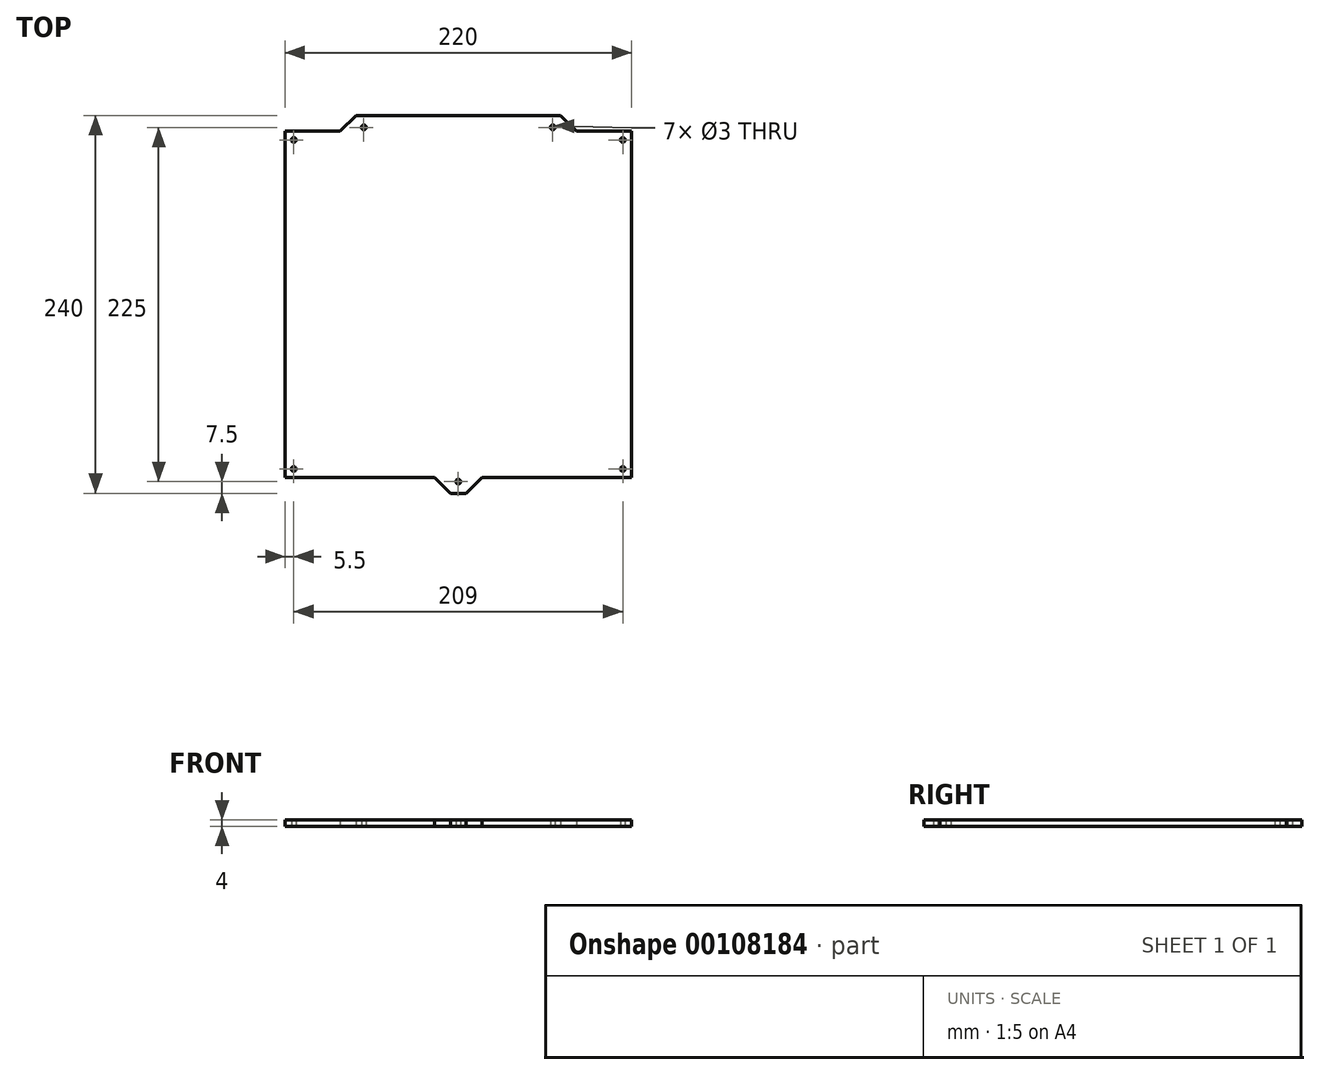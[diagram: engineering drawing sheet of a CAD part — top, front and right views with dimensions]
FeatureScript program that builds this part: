
annotation { "Feature Type Name" : "Feature", "Feature Type Description" : "" }
export const myFeature = defineFeature(function(context is Context, id is Id, definition is map)
    precondition{}
    {
        {
            var Q0;
            Q0=qCreatedBy(makeId("Top.planeOp"),FACE);
            var sketch = newSketch(context, id + "F0", { "sketchPlane" : qUnion([Q0])});
            skLineSegment(sketch, "E0.bottom", {"start": v(-110, 110) * mm, "end": v(-75, 110) * mm});
            skLineSegment(sketch, "E0.top", {"start": v(-110, -110) * mm, "end": v(-15, -110) * mm});
            skLineSegment(sketch, "E0.left", {"start": v(-110, 110) * mm, "end": v(-110, -110) * mm});
            skPoint(sketch, "E0.middle", {"position": v(0, 0) * mm});
            skLineSegment(sketch, "E1", {"start": v(0, 120) * mm, "end": v(-65, 120) * mm});
            skLineSegment(sketch, "E2", {"start": v(-65, 120) * mm, "end": v(-75, 110) * mm});
            skLineSegment(sketch, "E3", {"start": v(0, -120) * mm, "end": v(-5, -120) * mm});
            skLineSegment(sketch, "E4", {"start": v(-5, -120) * mm, "end": v(-15, -110) * mm});
            skCircle(sketch, "E5", {"center": v(0, -112.5) * mm, "radius": 1.5 * mm});
            skCircle(sketch, "E6", {"center": v(-60, 112.5) * mm, "radius": 1.5 * mm});
            skCircle(sketch, "E7.MirrorC", {"center": v(60, 112.5) * mm, "radius": 1.5 * mm});
            skLineSegment(sketch, "E8.MirrorCS", {"start": v(0, 120) * mm, "end": v(65, 120) * mm});
            skLineSegment(sketch, "E9.MirrorCS", {"start": v(65, 120) * mm, "end": v(75, 110) * mm});
            skLineSegment(sketch, "E10.MirrorCS", {"start": v(110, 110) * mm, "end": v(75, 110) * mm});
            skLineSegment(sketch, "E11.MirrorCS", {"start": v(110, 110) * mm, "end": v(110, -110) * mm});
            skLineSegment(sketch, "E12.MirrorCS", {"start": v(110, -110) * mm, "end": v(15, -110) * mm});
            skLineSegment(sketch, "E13.MirrorCS", {"start": v(0, -120) * mm, "end": v(5, -120) * mm});
            skLineSegment(sketch, "E14.MirrorCS", {"start": v(5, -120) * mm, "end": v(15, -110) * mm});
            skCircle(sketch, "E15", {"center": v(-104.5, 104.5) * mm, "radius": 1.5 * mm});
            skCircle(sketch, "E16.MirrorC", {"center": v(104.5, 104.5) * mm, "radius": 1.5 * mm});
            skCircle(sketch, "E17.MirrorC", {"center": v(-104.5, -104.5) * mm, "radius": 1.5 * mm});
            skCircle(sketch, "E18.MirrorC", {"center": v(104.5, -104.5) * mm, "radius": 1.5 * mm});
            skSolve(sketch);
        }
        {
            var Q0;
            {var subQ1=sQuery(id+"F0.wireOp",EDGE,"E0.left");Q0=makeQuery(id+"F0.imprint","IMPRINT",FACE,{"disambiguationData":[TD([[makeQuery(id+"F0.imprint","IMPRINT",EDGE,{"derivedFrom":subQ1}),1.0]])]});}
            var Q1;
            Q1=makeQuery(id+"F0.imprint","IMPRINT",FACE,{"disambiguationData":[TD([[makeQuery(id+"F0.imprint","IMPRINT",EDGE,{"derivedFrom":sQuery(id+"F0.wireOp",EDGE,"E1")}),1.0]])]});
            var Q2;
            Q2=makeQuery(id+"F0.imprint","IMPRINT",FACE,{"disambiguationData":[TD([[makeQuery(id+"F0.imprint","IMPRINT",EDGE,{"derivedFrom":sQuery(id+"F0.wireOp",EDGE,"E3")}),-1.0]])]});
            extrude(context, id + "F1", {"entities" : qUnion([Q0, Q1, Q2]), "depth" : 4 * mm});
        }
    });
